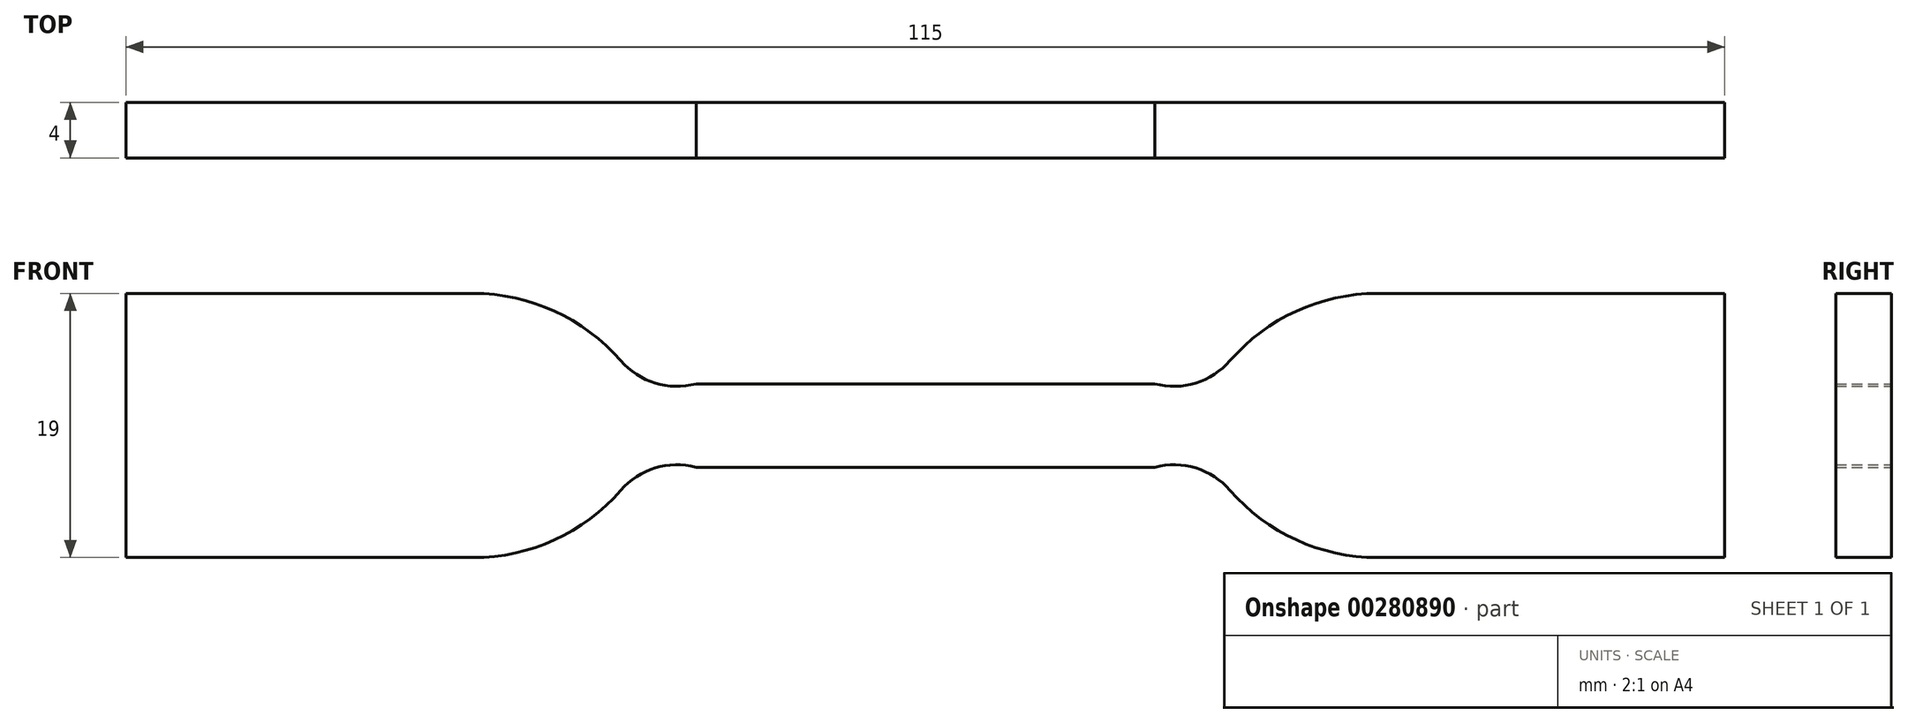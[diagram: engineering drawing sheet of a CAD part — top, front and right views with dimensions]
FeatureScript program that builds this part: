
annotation { "Feature Type Name" : "Feature", "Feature Type Description" : "" }
export const myFeature = defineFeature(function(context is Context, id is Id, definition is map)
    precondition{}
    {
        {
            var Q0;
            Q0=qCreatedBy(makeId("Front.planeOp"),FACE);
            var sketch = newSketch(context, id + "F0", { "sketchPlane" : qUnion([Q0])});
            skLineSegment(sketch, "E0", {"start": v(0, 3) * mm, "end": v(16.5, 3) * mm});
            skLineSegment(sketch, "E1", {"start": v(32.5, 9.5) * mm, "end": v(57.5, 9.5) * mm});
            skLineSegment(sketch, "E2.MirrorCS", {"start": v(0, -3) * mm, "end": v(16.5, -3) * mm});
            skLineSegment(sketch, "E3.MirrorCS", {"start": v(32.5, -9.5) * mm, "end": v(57.5, -9.5) * mm});
            skLineSegment(sketch, "E4.MirrorCS", {"start": v(0, 3) * mm, "end": v(-16.5, 3) * mm});
            skLineSegment(sketch, "E5.MirrorCS", {"start": v(-32.5, 9.5) * mm, "end": v(-57.5, 9.5) * mm});
            skLineSegment(sketch, "E6.MirrorCS", {"start": v(0, -3) * mm, "end": v(-16.5, -3) * mm});
            skLineSegment(sketch, "E7.MirrorCS", {"start": v(-32.5, -9.5) * mm, "end": v(-57.5, -9.5) * mm});
            skLineSegment(sketch, "E8", {"start": v(-57.5, 9.5) * mm, "end": v(-57.5, -9.5) * mm});
            skLineSegment(sketch, "E9", {"start": v(57.5, 9.5) * mm, "end": v(57.5, -9.5) * mm});
            skArc(sketch, "E10", {"start": v(-32.5, 9.5) * mm, "mid": v(-26.68, 8.23) * mm, "end": v(-21.92, 4.66) * mm});
            skArc(sketch, "E11", {"start": v(-21.92, 4.66) * mm, "mid": v(-19.45, 3.05) * mm, "end": v(-16.5, 3) * mm});
            skArc(sketch, "E12.MirrorCS", {"start": v(-32.5, -9.5) * mm, "mid": v(-26.68, -8.23) * mm, "end": v(-21.92, -4.66) * mm});
            skArc(sketch, "E13.MirrorCS", {"start": v(-21.92, -4.66) * mm, "mid": v(-19.45, -3.05) * mm, "end": v(-16.5, -3) * mm});
            skArc(sketch, "E14.MirrorCS", {"start": v(21.92, -4.66) * mm, "mid": v(19.45, -3.05) * mm, "end": v(16.5, -3) * mm});
            skArc(sketch, "E15.MirrorCS", {"start": v(21.92, 4.66) * mm, "mid": v(19.45, 3.05) * mm, "end": v(16.5, 3) * mm});
            skArc(sketch, "E16.MirrorCS", {"start": v(32.5, 9.5) * mm, "mid": v(26.68, 8.23) * mm, "end": v(21.92, 4.66) * mm});
            skArc(sketch, "E17.MirrorCS", {"start": v(32.5, -9.5) * mm, "mid": v(26.68, -8.23) * mm, "end": v(21.92, -4.66) * mm});
            skSolve(sketch);
        }
        {
            var Q0;
            Q0 = qSketchRegion(id + "F0", true);
            extrude(context, id + "F1", {"entities" : qUnion([Q0]), "endBound" : BoundingType.SYMMETRIC, "depth" : 4 * mm});
        }
        {
            var Q0;
            Q0 = qSketchRegion(id + "F0", true);
            extrude(context, id + "F2", {"entities" : qUnion([Q0]), "operationType" : NewBodyOperationType.ADD, "endBound" : BoundingType.SYMMETRIC, "depth" : 4 * mm});
        }
    });
